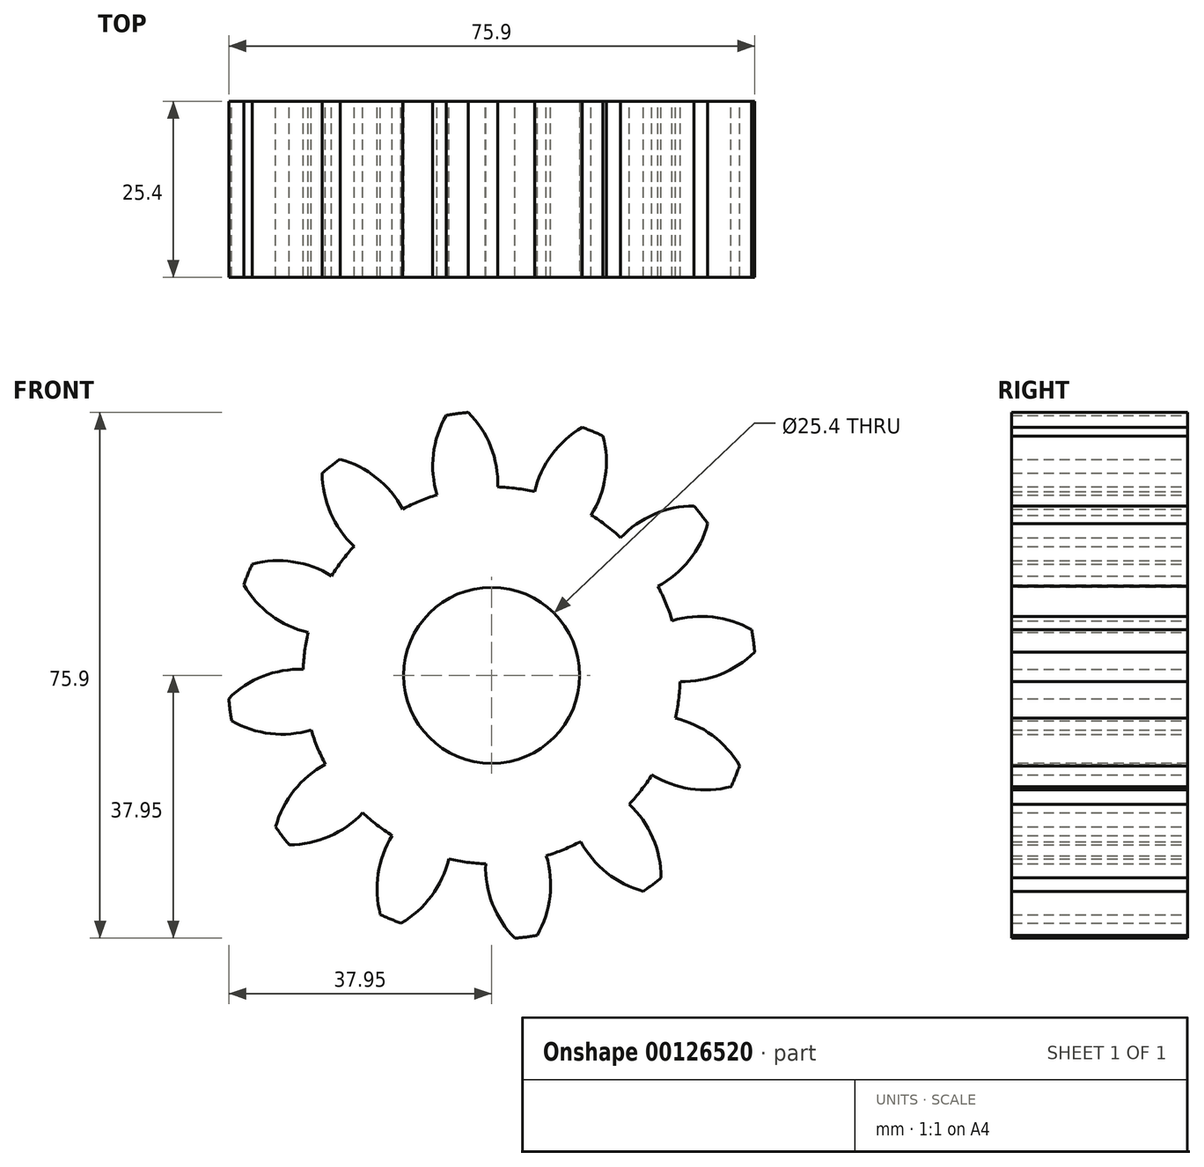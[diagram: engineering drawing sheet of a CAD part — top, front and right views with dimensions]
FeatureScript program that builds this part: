
annotation { "Feature Type Name" : "Feature", "Feature Type Description" : "" }
export const myFeature = defineFeature(function(context is Context, id is Id, definition is map)
    precondition{}
    {
        {
            assignVariable(context, id + "F0", {"name" : "NOT", "anyValue" : 12});
        }
        {
            var Q0;
            Q0=qCreatedBy(makeId("Front.planeOp"),FACE);
            var sketch = newSketch(context, id + "F1", { "sketchPlane" : qUnion([Q0])});
            skCircle(sketch, "E0", {"center": v(0, 0) * mm, "radius": 38.1 * mm});
            skCircle(sketch, "E1", {"center": v(0, 0) * mm, "radius": 32.66 * mm});
            skCircle(sketch, "E2", {"center": v(0, 0) * mm, "radius": 27.21 * mm});
            skLineSegment(sketch, "E3", {"start": v(0, 0) * mm, "end": v(0, 56.5) * mm});
            skLineSegment(sketch, "E4", {"start": v(0, 0) * mm, "end": v(-7.42, 56.35) * mm});
            skLineSegment(sketch, "E5", {"start": v(0, 32.66) * mm, "end": v(-56.68, 32.66) * mm});
            skLineSegment(sketch, "E6", {"start": v(0, 32.66) * mm, "end": v(-52.94, 13.39) * mm});
            skCircle(sketch, "E7", {"center": v(0, 32.66) * mm, "radius": 14.6 * mm});
            skArc(sketch, "E8", {"start": v(0.87, 27.2) * mm, "mid": v(-0.13, 33.01) * mm, "end": v(-3.36, 37.95) * mm});
            skArc(sketch, "E9.MirrorCS", {"start": v(-7.88, 26.05) * mm, "mid": v(-8.41, 31.92) * mm, "end": v(-6.58, 37.53) * mm});
            skSolve(sketch);
        }
        {
            var Q0;
            {var subQ0=sQuery(id+"F1.wireOp",EDGE,"E3");var subQ1=sQuery(id+"F1.wireOp",EDGE,"E2");var subQ2=makeQuery(id+"F1.imprint","INTERSECT",VERTEX,{"derivedFrom":[subQ1,subQ0]});Q0=makeQuery(id+"F1.imprint","IMPRINT",FACE,{"disambiguationData":[TD([[makeQuery(id+"F1.imprint","IMPRINT",EDGE,{"disambiguationData":[TD([[subQ2,-1.0]])],"derivedFrom":subQ1}),-1.0]])]});}
            var Q1;
            {var subQ0=sQuery(id+"F1.wireOp",EDGE,"E9.MirrorCS");var subQ1=sQuery(id+"F1.wireOp",EDGE,"E2");var subQ2=makeQuery(id+"F1.imprint","INTERSECT",VERTEX,{"derivedFrom":[subQ1,subQ0]});Q1=makeQuery(id+"F1.imprint","IMPRINT",FACE,{"disambiguationData":[TD([[makeQuery(id+"F1.imprint","IMPRINT",EDGE,{"disambiguationData":[TD([[subQ2,1.0]])],"derivedFrom":subQ1}),-1.0]])]});}
            var Q2;
            {var subQ0=sQuery(id+"F1.wireOp",EDGE,"E4");var subQ1=sQuery(id+"F1.wireOp",EDGE,"E1");var subQ2=makeQuery(id+"F1.imprint","INTERSECT",VERTEX,{"derivedFrom":[subQ1,subQ0]});Q2=makeQuery(id+"F1.imprint","IMPRINT",FACE,{"disambiguationData":[TD([[makeQuery(id+"F1.imprint","IMPRINT",EDGE,{"disambiguationData":[TD([[subQ2,-1.0]])],"derivedFrom":subQ1}),1.0]])]});}
            var Q3;
            {var subQ0=sQuery(id+"F1.wireOp",EDGE,"E4");var subQ1=sQuery(id+"F1.wireOp",EDGE,"E1");var subQ2=makeQuery(id+"F1.imprint","INTERSECT",VERTEX,{"derivedFrom":[subQ1,subQ0]});Q3=makeQuery(id+"F1.imprint","IMPRINT",FACE,{"disambiguationData":[TD([[makeQuery(id+"F1.imprint","IMPRINT",EDGE,{"disambiguationData":[TD([[subQ2,-1.0]])],"derivedFrom":subQ1}),-1.0]])]});}
            var Q4;
            {var subQ1=sQuery(id+"F1.wireOp",EDGE,"E1");var subQ3=sQuery(id+"F1.wireOp",EDGE,"E4");var subQ4=makeQuery(id+"F1.imprint","INTERSECT",VERTEX,{"derivedFrom":[subQ1,subQ3]});Q4=makeQuery(id+"F1.imprint","IMPRINT",FACE,{"disambiguationData":[TD([[makeQuery(id+"F1.imprint","IMPRINT",EDGE,{"disambiguationData":[TD([[subQ4,1.0]])],"derivedFrom":subQ3}),-1.0]])]});}
            var Q5;
            {var subQ1=sQuery(id+"F1.wireOp",EDGE,"E1");var subQ3=sQuery(id+"F1.wireOp",EDGE,"E4");var subQ4=makeQuery(id+"F1.imprint","INTERSECT",VERTEX,{"derivedFrom":[subQ1,subQ3]});Q5=makeQuery(id+"F1.imprint","IMPRINT",FACE,{"disambiguationData":[TD([[makeQuery(id+"F1.imprint","IMPRINT",EDGE,{"disambiguationData":[TD([[subQ4,-1.0]])],"derivedFrom":subQ3}),-1.0]])]});}
            var Q6;
            {var subQ0=sQuery(id+"F1.wireOp",EDGE,"E8");var subQ1=sQuery(id+"F1.wireOp",EDGE,"E0");var subQ2=makeQuery(id+"F1.imprint","INTERSECT",VERTEX,{"derivedFrom":[subQ1,subQ0]});Q6=makeQuery(id+"F1.imprint","IMPRINT",FACE,{"disambiguationData":[TD([[makeQuery(id+"F1.imprint","IMPRINT",EDGE,{"disambiguationData":[TD([[subQ2,-1.0]])],"derivedFrom":subQ1}),1.0]])]});}
            var Q7;
            {var subQ0=sQuery(id+"F1.wireOp",EDGE,"E9.MirrorCS");var subQ1=sQuery(id+"F1.wireOp",EDGE,"E0");var subQ2=makeQuery(id+"F1.imprint","INTERSECT",VERTEX,{"derivedFrom":[subQ1,subQ0]});Q7=makeQuery(id+"F1.imprint","IMPRINT",FACE,{"disambiguationData":[TD([[makeQuery(id+"F1.imprint","IMPRINT",EDGE,{"disambiguationData":[TD([[subQ2,1.0]])],"derivedFrom":subQ1}),1.0]])]});}
            var Q8;
            {var subQ0=sQuery(id+"F1.wireOp",EDGE,"E8");var subQ1=sQuery(id+"F1.wireOp",EDGE,"E2");var subQ2=makeQuery(id+"F1.imprint","INTERSECT",VERTEX,{"derivedFrom":[subQ1,subQ0]});Q8=makeQuery(id+"F1.imprint","IMPRINT",FACE,{"disambiguationData":[TD([[makeQuery(id+"F1.imprint","IMPRINT",EDGE,{"disambiguationData":[TD([[subQ2,-1.0]])],"derivedFrom":subQ1}),-1.0]])]});}
            var Q9;
            {var subQ0=sQuery(id+"F1.wireOp",EDGE,"E7");var subQ1=sQuery(id+"F1.wireOp",EDGE,"E2");var subQ8=makeQuery(id+"F1.imprint","INTERSECT",VERTEX,{"disambiguationData":[OD(0.0)],"derivedFrom":[subQ1,subQ0]});Q9=makeQuery(id+"F1.imprint","IMPRINT",FACE,{"disambiguationData":[TD([[makeQuery(id+"F1.imprint","IMPRINT",EDGE,{"disambiguationData":[TD([[subQ8,1.0]])],"derivedFrom":subQ1}),1.0]])]});}
            var Q10;
            {var subQ0=sQuery(id+"F1.wireOp",EDGE,"E2");var subQ1=makeQuery(id+"F1.imprint","INTERSECT",VERTEX,{"derivedFrom":[subQ0,sQuery(id+"F1.wireOp",EDGE,"E9.MirrorCS")]});Q10=makeQuery(id+"F1.imprint","IMPRINT",FACE,{"disambiguationData":[TD([[makeQuery(id+"F1.imprint","IMPRINT",EDGE,{"disambiguationData":[TD([[subQ1,1.0]])],"derivedFrom":subQ0}),1.0]])]});}
            var Q11;
            {var subQ0=sQuery(id+"F1.wireOp",EDGE,"E3");var subQ1=sQuery(id+"F1.wireOp",EDGE,"E2");var subQ2=makeQuery(id+"F1.imprint","INTERSECT",VERTEX,{"derivedFrom":[subQ1,subQ0]});Q11=makeQuery(id+"F1.imprint","IMPRINT",FACE,{"disambiguationData":[TD([[makeQuery(id+"F1.imprint","IMPRINT",EDGE,{"disambiguationData":[TD([[subQ2,-1.0]])],"derivedFrom":subQ1}),1.0]])]});}
            var Q12;
            {var subQ0=sQuery(id+"F1.wireOp",EDGE,"E4");var subQ1=sQuery(id+"F1.wireOp",EDGE,"E3");var subQ2=makeQuery(id+"F1.imprint","INTERSECT",VERTEX,{"derivedFrom":[subQ1,subQ0]});Q12=makeQuery(id+"F1.imprint","IMPRINT",FACE,{"disambiguationData":[TD([[makeQuery(id+"F1.imprint","IMPRINT",EDGE,{"disambiguationData":[TD([[subQ2,-1.0]])],"derivedFrom":subQ1}),1.0]])]});}
            var Q13;
            {var subQ0=sQuery(id+"F1.wireOp",EDGE,"E2");var subQ1=makeQuery(id+"F1.imprint","INTERSECT",VERTEX,{"derivedFrom":[subQ0,sQuery(id+"F1.wireOp",EDGE,"E8")]});Q13=makeQuery(id+"F1.imprint","IMPRINT",FACE,{"disambiguationData":[TD([[makeQuery(id+"F1.imprint","IMPRINT",EDGE,{"disambiguationData":[TD([[subQ1,1.0]])],"derivedFrom":subQ0}),1.0]])]});}
            extrude(context, id + "F2", {"entities" : qUnion([Q0, Q1, Q2, Q3, Q4, Q5, Q6, Q7, Q8, Q9, Q10, Q11, Q12, Q13]), "endBound" : BoundingType.SYMMETRIC, "depth" : 25.4 * mm});
        }
        {
            var Q0;
            Q0=makeQuery(id+"F2.opExtrude","SWEPT_BODY",BODY,{"disambiguationData":[OSD([sQuery(id+"F1.wireOp",EDGE,"E0"),sQuery(id+"F1.wireOp",EDGE,"E2"),sQuery(id+"F1.wireOp",EDGE,"E8"),sQuery(id+"F1.wireOp",EDGE,"E9.MirrorCS")])]});
            var Q1;
            Q1=makeQuery(id+"F2.opExtrude","SWEPT_FACE",FACE,{"disambiguationData":[OSD([sQuery(id+"F1.wireOp",EDGE,"E2")])]});
            circularPattern(context, id + "F3", {"operationType" : NewBodyOperationType.ADD, "entities" : qUnion([Q0]), "axis" : qUnion([Q1]), "angle" : (360 / getVariable(context, 'NOT')) * degree, "instanceCount" : getVariable(context, 'NOT')});
        }
        {
            var Q0;
            {var subQ0=makeQuery(id+"F2.opExtrude","CAP_FACE",FACE,{"disambiguationData":[OSD([sQuery(id+"F1.wireOp",EDGE,"E0"),sQuery(id+"F1.wireOp",EDGE,"E2"),sQuery(id+"F1.wireOp",EDGE,"E8"),sQuery(id+"F1.wireOp",EDGE,"E9.MirrorCS")])],"isStart":false});Q0=makeQuery(id+"F3.boolean.opBoolean","MERGE",FACE,{"derivedFrom":[subQ0,makeQuery(id+"F3.opPattern","COPY",FACE,{"derivedFrom":subQ0,"instanceName":"1"}),makeQuery(id+"F3.opPattern","COPY",FACE,{"derivedFrom":subQ0,"instanceName":"2"}),makeQuery(id+"F3.opPattern","COPY",FACE,{"derivedFrom":subQ0,"instanceName":"3"}),makeQuery(id+"F3.opPattern","COPY",FACE,{"derivedFrom":subQ0,"instanceName":"4"}),makeQuery(id+"F3.opPattern","COPY",FACE,{"derivedFrom":subQ0,"instanceName":"5"}),makeQuery(id+"F3.opPattern","COPY",FACE,{"derivedFrom":subQ0,"instanceName":"6"}),makeQuery(id+"F3.opPattern","COPY",FACE,{"derivedFrom":subQ0,"instanceName":"7"}),makeQuery(id+"F3.opPattern","COPY",FACE,{"derivedFrom":subQ0,"instanceName":"8"}),makeQuery(id+"F3.opPattern","COPY",FACE,{"derivedFrom":subQ0,"instanceName":"9"}),makeQuery(id+"F3.opPattern","COPY",FACE,{"derivedFrom":subQ0,"instanceName":"10"}),makeQuery(id+"F3.opPattern","COPY",FACE,{"derivedFrom":subQ0,"instanceName":"11"})]});}
            var sketch = newSketch(context, id + "F4", { "sketchPlane" : qUnion([Q0])});
            skPoint(sketch, "E10", {"position": v(0, 0) * mm});
            skSolve(sketch);
        }
        {
            var Q0;
            Q0=sQuery(id+"F4.wireOp",VERTEX,"E10");
            var Q1;
            Q1=makeQuery(id+"F2.opExtrude","SWEPT_BODY",BODY,{"disambiguationData":[OSD([sQuery(id+"F1.wireOp",EDGE,"E0"),sQuery(id+"F1.wireOp",EDGE,"E2"),sQuery(id+"F1.wireOp",EDGE,"E8"),sQuery(id+"F1.wireOp",EDGE,"E9.MirrorCS")])]});
            hole(context, id + "F5", {"style" : HoleStyle.SIMPLE, "holeDiameter" : 25.4 * mm, "endStyle" : HoleEndStyle.THROUGH, "locations" : qUnion([Q0]), "scope" : qUnion([Q1])});
        }
    });
